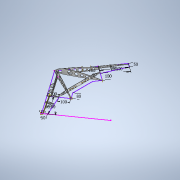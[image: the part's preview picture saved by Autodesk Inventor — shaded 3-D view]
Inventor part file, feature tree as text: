
AUTODESK INVENTOR PART (.ipt)
format: ipt  version: 2020 (Build 240168000, 168)  size: 897,536 bytes
history: native  units: mm
features: sketch x14, other x11, extrude x9, mirror x1
ambient origin geometry x8: Origin, YZ Plane, XZ Plane, XY Plane, X Axis, Y Axis, Z Axis, Center Point
bodies: Solide1 (feature_tree)
feature tree (35):
  sketch  "Esquisse1"
  other  "Plan de construction11"
  sketch  "Esquisse3"
  other  "Plan de construction9"
  sketch  "Esquisse6"
  other  "Plan de construction10"
  sketch  "Esquisse7"
  other  "Plan de construction12"
  sketch  "Esquisse9"
  other  "Plan de construction4"
  extrude  "Extrusion4"  Depth=50.0mm
  extrude  "Extrusion5"  TaperAngle=90.0deg  [1 undecoded]
  extrude  "Extrusion6"  Depth=50.0mm
  other  "Plan de construction5"
  sketch  "Esquisse12"
  extrude  "Extrusion7"  TaperAngle=90.0deg  [1 undecoded]
  sketch  "Esquisse 3D4"
  extrude  "Extrusion8"  Depth=250.0mm
  other  "Plan de construction8"
  extrude  "Extrusion9"  Depth=100.0mm
  extrude  "Extrusion10"  Depth=250.0mm
  other  "Plan de construction13"
  extrude  "Extrusion11"  Depth=100.0mm
  other  "Plan de construction14"
  extrude  "Extrusion12"  Depth=100.0mm
  mirror  "Symétrie4"
  sketch  "Esquisse10"
  sketch  "Esquisse11"
  other  "Plan de construction6"
  other  "Plan de construction7"
  sketch  "Esquisse14"
  sketch  "Esquisse17"
  sketch  "Esquisse18"
  sketch  "Esquisse19"
  sketch  "Esquisse20"
note: 2 required parameter values undecoded (feature->parameter linkage not recoverable at this tier; creation-order binding heuristic only, values carry confidence <= 0.55)
